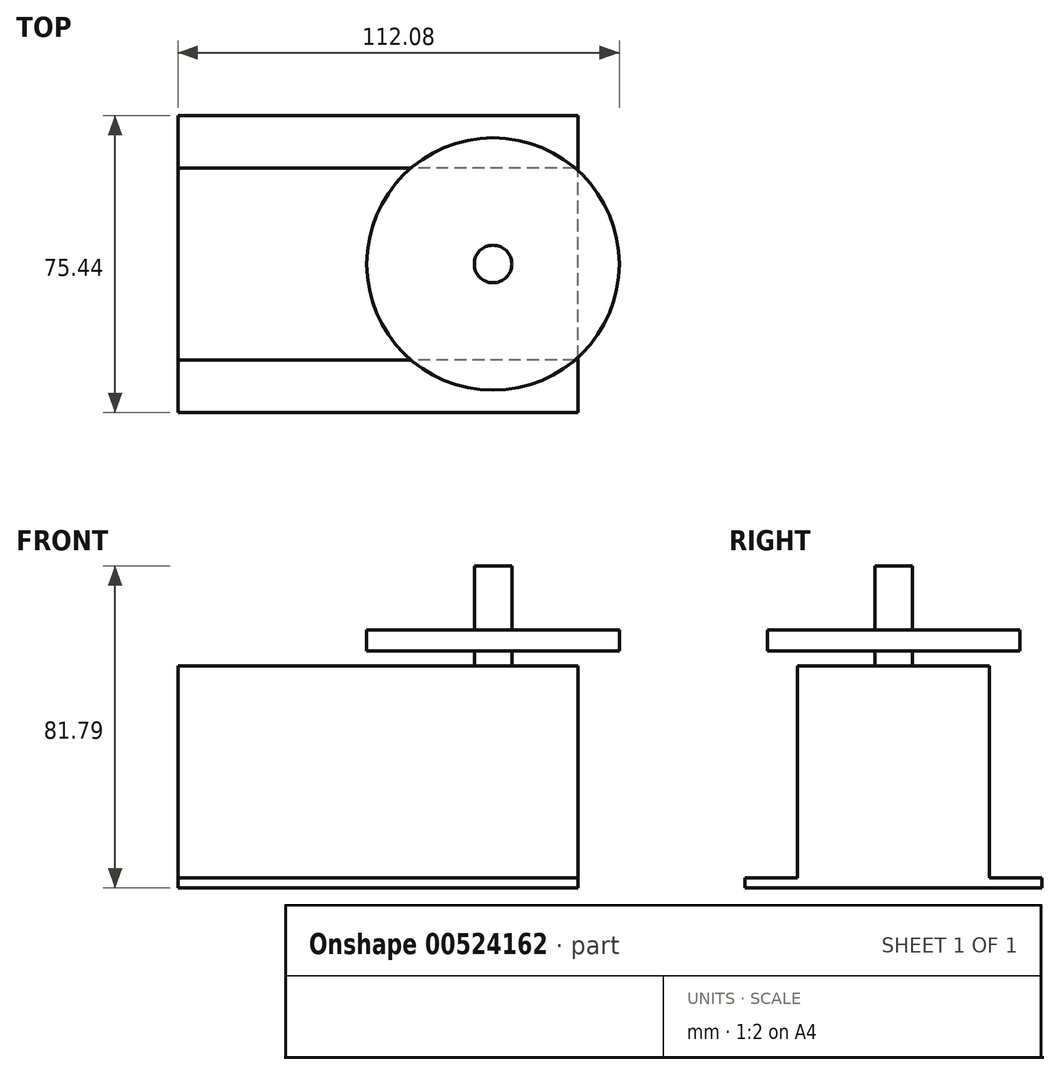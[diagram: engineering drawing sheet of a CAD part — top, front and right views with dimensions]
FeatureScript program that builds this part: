
annotation { "Feature Type Name" : "Feature", "Feature Type Description" : "" }
export const myFeature = defineFeature(function(context is Context, id is Id, definition is map)
    precondition{}
    {
        {
            var Q0;
            Q0=qCreatedBy(makeId("Top.planeOp"),FACE);
            var sketch = newSketch(context, id + "F0", { "sketchPlane" : qUnion([Q0])});
            skLineSegment(sketch, "E0.bottom", {"start": v(50.8, -37.72) * mm, "end": v(-50.8, -37.72) * mm});
            skLineSegment(sketch, "E0.top", {"start": v(50.8, 37.72) * mm, "end": v(-50.8, 37.72) * mm});
            skLineSegment(sketch, "E0.left", {"start": v(50.8, -37.72) * mm, "end": v(50.8, 37.72) * mm});
            skLineSegment(sketch, "E0.right", {"start": v(-50.8, -37.72) * mm, "end": v(-50.8, 37.72) * mm});
            skPoint(sketch, "E0.middle", {"position": v(0, 0) * mm});
            skLineSegment(sketch, "E1.bottom", {"start": v(50.8, -24.38) * mm, "end": v(-50.8, -24.38) * mm});
            skLineSegment(sketch, "E1.top", {"start": v(50.8, 24.38) * mm, "end": v(-50.8, 24.38) * mm});
            skLineSegment(sketch, "E1.left", {"start": v(50.8, -24.38) * mm, "end": v(50.8, 24.38) * mm});
            skLineSegment(sketch, "E1.right", {"start": v(-50.8, -24.38) * mm, "end": v(-50.8, 24.38) * mm});
            skSolve(sketch);
        }
        {
            var Q0;
            Q0=makeQuery(id+"F0.imprint","IMPRINT",FACE,{"disambiguationData":[TD([[makeQuery(id+"F0.imprint","IMPRINT",EDGE,{"derivedFrom":sQuery(id+"F0.wireOp",EDGE,"E1.bottom")}),-1.0]])]});
            extrude(context, id + "F1", {"entities" : qUnion([Q0]), "depth" : 56.4 * mm});
        }
        {
            var Q0;
            {var subQ0=sQuery(id+"F0.wireOp",EDGE,"E0.top");Q0=makeQuery(id+"F0.imprint","IMPRINT",FACE,{"disambiguationData":[TD([[makeQuery(id+"F0.imprint","IMPRINT",EDGE,{"derivedFrom":subQ0}),1.0]])]});}
            var Q1;
            {var subQ0=sQuery(id+"F0.wireOp",EDGE,"E0.bottom");Q1=makeQuery(id+"F0.imprint","IMPRINT",FACE,{"disambiguationData":[TD([[makeQuery(id+"F0.imprint","IMPRINT",EDGE,{"derivedFrom":subQ0}),-1.0]])]});}
            extrude(context, id + "F2", {"entities" : qUnion([Q0, Q1]), "operationType" : NewBodyOperationType.ADD, "depth" : 2.54 * mm});
        }
        {
            var Q0;
            Q0=makeQuery(id+"F1.opExtrude","CAP_FACE",FACE,{"disambiguationData":[OSD([sQuery(id+"F0.wireOp",EDGE,"E1.bottom"),sQuery(id+"F0.wireOp",EDGE,"E1.top"),sQuery(id+"F0.wireOp",EDGE,"E1.left"),sQuery(id+"F0.wireOp",EDGE,"E1.right")])],"isStart":false});
            var sketch = newSketch(context, id + "F3", { "sketchPlane" : qUnion([Q0])});
            skCircle(sketch, "E2", {"center": v(29.21, 0) * mm, "radius": 4.76 * mm});
            skPoint(sketch, "E2.centerSnap0", {"position": v(50.8, 0) * mm});
            skCircle(sketch, "E3", {"center": v(29.21, 0) * mm, "radius": 32.07 * mm});
            skSolve(sketch);
        }
        {
            var Q0;
            Q0=makeQuery(id+"F3.imprint","IMPRINT",FACE,{"disambiguationData":[TD([[makeQuery(id+"F3.imprint","IMPRINT",EDGE,{"derivedFrom":sQuery(id+"F3.wireOp",EDGE,"E2")}),1.0]])]});
            extrude(context, id + "F4", {"entities" : qUnion([Q0]), "operationType" : NewBodyOperationType.ADD, "depth" : 25.4 * mm});
        }
        {
            var Q0;
            Q0=qSketchRegion(id+"F3",true);
            extrude(context, id + "F5", {"entities" : qUnion([Q0]), "operationType" : NewBodyOperationType.ADD, "depth" : 9.14 * mm});
        }
        {
            var Q0;
            Q0=qSketchRegion(id+"F3",true);
            extrude(context, id + "F6", {"entities" : qUnion([Q0]), "operationType" : NewBodyOperationType.REMOVE, "depth" : 3.8 * mm});
        }
    });
